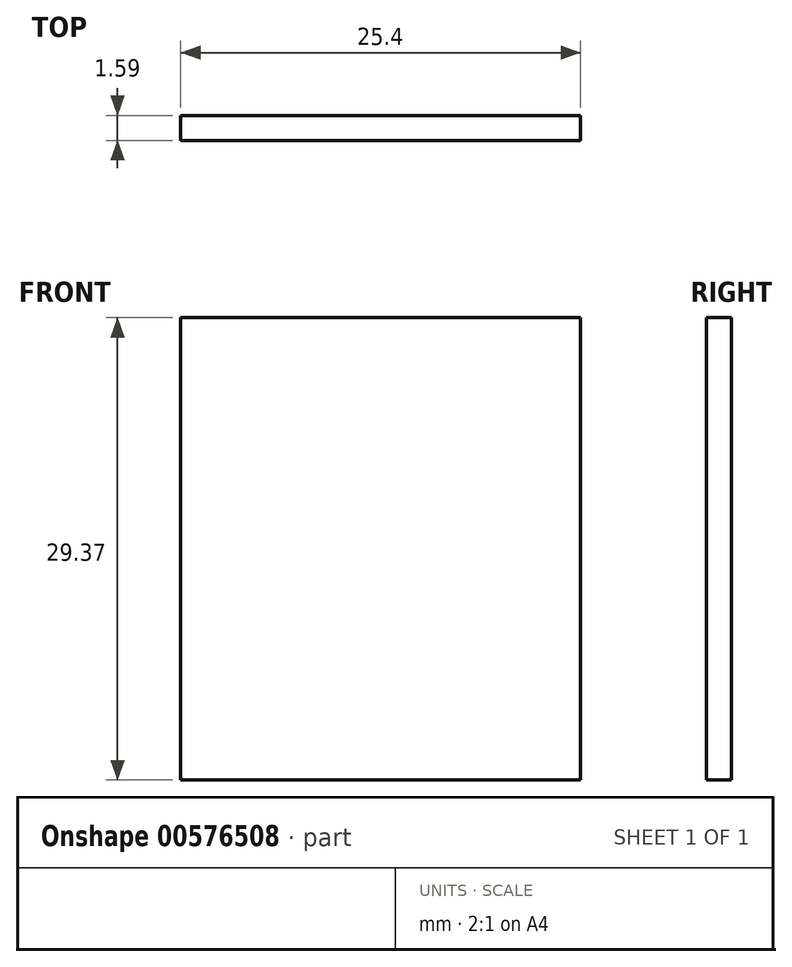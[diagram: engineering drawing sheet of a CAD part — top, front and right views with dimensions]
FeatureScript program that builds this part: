
annotation { "Feature Type Name" : "Feature", "Feature Type Description" : "" }
export const myFeature = defineFeature(function(context is Context, id is Id, definition is map)
    precondition{}
    {
        {
            var Q0;
            Q0=qCreatedBy(makeId("Front.planeOp"),FACE);
            var sketch = newSketch(context, id + "F0", { "sketchPlane" : qUnion([Q0])});
            skLineSegment(sketch, "E0.bottom", {"start": v(12.7, 13.5) * mm, "end": v(-12.7, 13.5) * mm});
            skLineSegment(sketch, "E0.top", {"start": v(12.7, -13.5) * mm, "end": v(-12.7, -13.5) * mm});
            skLineSegment(sketch, "E0.left", {"start": v(12.7, 13.5) * mm, "end": v(12.7, -13.5) * mm});
            skLineSegment(sketch, "E0.right", {"start": v(-12.7, 13.5) * mm, "end": v(-12.7, -13.5) * mm});
            skPoint(sketch, "E0.middle", {"position": v(0, 0) * mm});
            skSolve(sketch);
        }
        {
            var Q0;
            Q0=makeQuery(id+"F0.imprint","IMPRINT",FACE,{"disambiguationData":[TD([[makeQuery(id+"F0.imprint","IMPRINT",EDGE,{"derivedFrom":sQuery(id+"F0.wireOp",EDGE,"E0.bottom")}),1.0]])]});
            extrude(context, id + "F1", {"entities" : qUnion([Q0]), "depth" : 1.59 * mm, "offsetDistance" : 25.4 * mm});
        }
        {
            var Q0;
            Q0=makeQuery(id+"F1.opExtrude","SWEPT_FACE",FACE,{"disambiguationData":[OSD([sQuery(id+"F0.wireOp",EDGE,"E0.bottom")])]});
            extrude(context, id + "F2", {"entities" : qUnion([Q0]), "operationType" : NewBodyOperationType.ADD, "depth" : 2.38 * mm, "offsetDistance" : 25.4 * mm});
        }
    });
